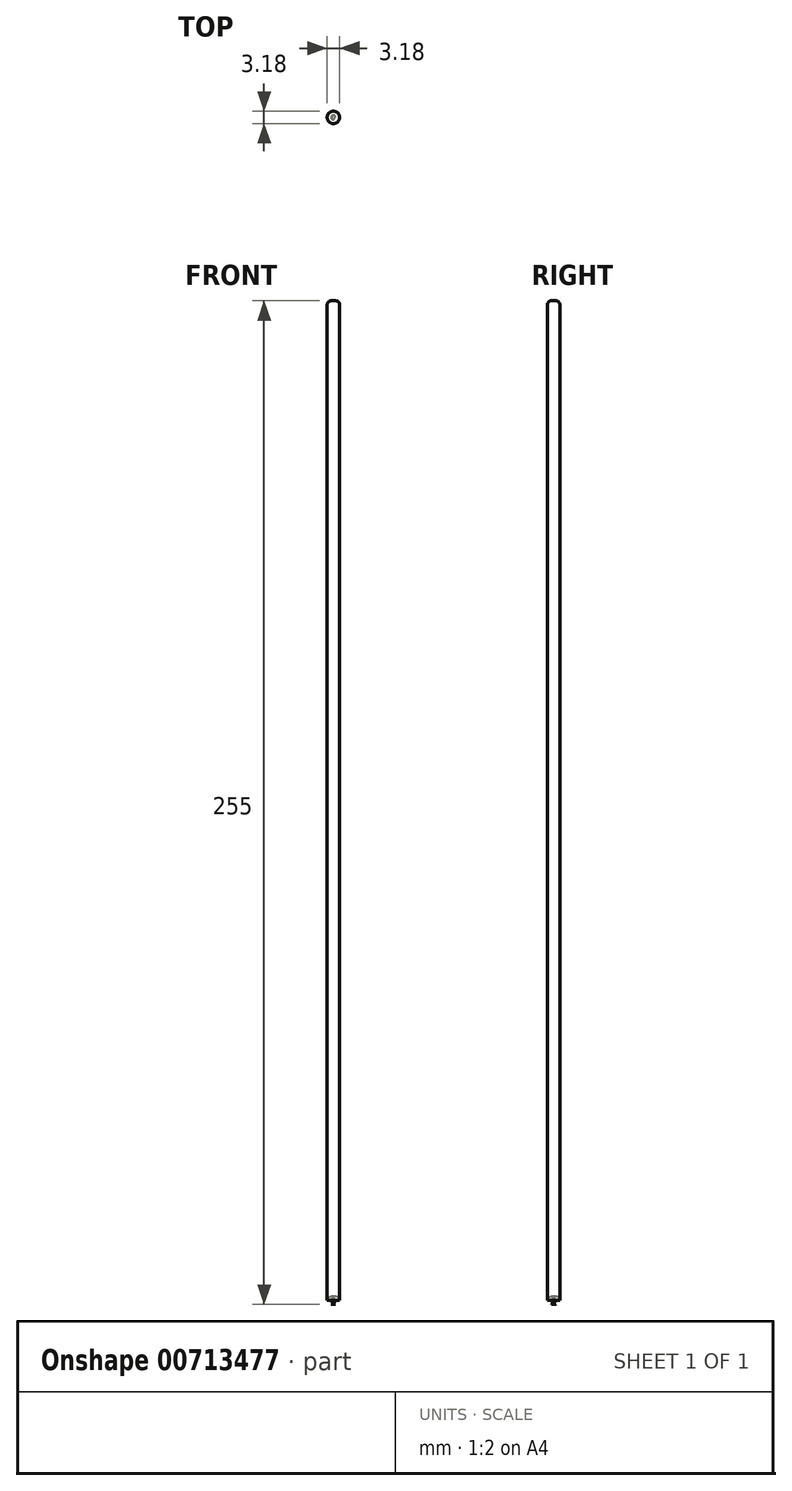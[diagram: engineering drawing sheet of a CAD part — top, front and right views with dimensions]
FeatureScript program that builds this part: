
annotation { "Feature Type Name" : "Feature", "Feature Type Description" : "" }
export const myFeature = defineFeature(function(context is Context, id is Id, definition is map)
    precondition{}
    {
        {
            assignVariable(context, id + "F0", {"name" : "length", "anyValue" : 255 * mm});
        }
        {
            var Q0;
            Q0=qCreatedBy(makeId("Top.planeOp"),FACE);
            var sketch = newSketch(context, id + "F1", { "sketchPlane" : qUnion([Q0])});
            skCircle(sketch, "E0", {"center": v(0, 0) * mm, "radius": 1.59 * mm});
            skSolve(sketch);
        }
        {
            var Q0;
            Q0 = qSketchRegion(id + "F1", true);
            extrude(context, id + "F2", {"entities" : qUnion([Q0]), "depth" : getVariable(context, 'length'), "offsetDistance" : 25 * mm});
        }
        {
            var Q0;
            Q0=makeQuery(id+"F2.opExtrude","CAP_EDGE",EDGE,{"disambiguationData":[OSD([sQuery(id+"F1.wireOp",EDGE,"E0")])],"isStart":true});
            var Q1;
            Q1=makeQuery(id+"F2.opExtrude","CAP_EDGE",EDGE,{"disambiguationData":[OSD([sQuery(id+"F1.wireOp",EDGE,"E0")])],"isStart":false});
            fillet(context, id + "F3", {"entities" : qUnion([Q0, Q1]), "radius" : 1 * mm, "tangentPropagation" : true, "allowEdgeOverflow" : false});
        }
    });
